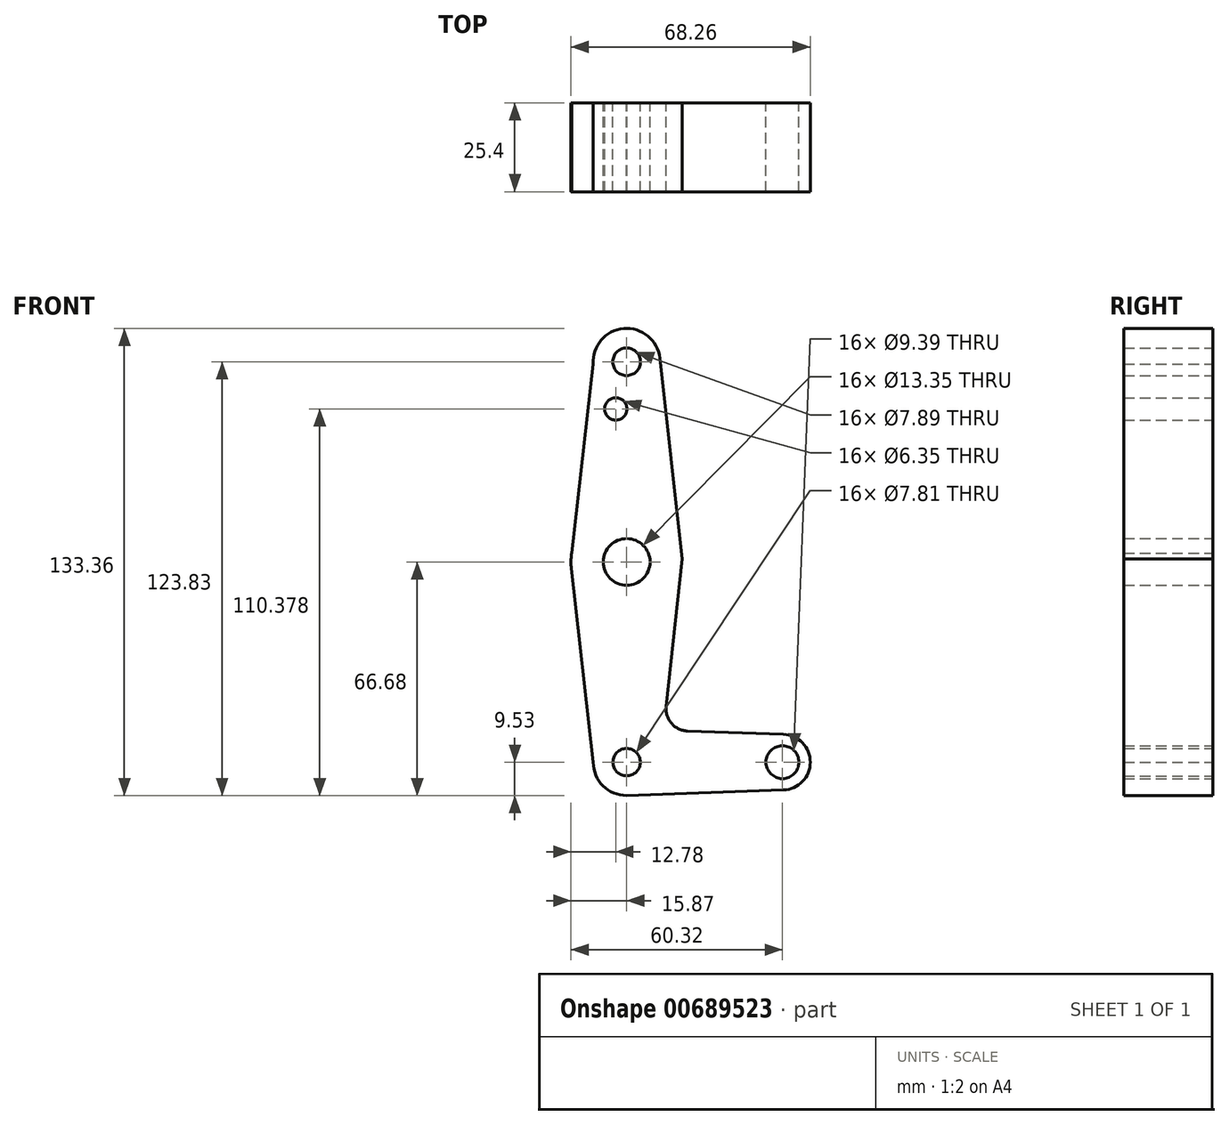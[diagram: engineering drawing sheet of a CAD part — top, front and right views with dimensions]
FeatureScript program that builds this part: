
annotation { "Feature Type Name" : "Feature", "Feature Type Description" : "" }
export const myFeature = defineFeature(function(context is Context, id is Id, definition is map)
    precondition{}
    {
        {
            var Q0;
            Q0=qCreatedBy(makeId("Front.planeOp"),FACE);
            var sketch = newSketch(context, id + "F0", { "sketchPlane" : qUnion([Q0])});
            skLineSegment(sketch, "E0", {"start": v(0, 0) * mm, "end": v(0, 114.3) * mm, "construction": true});
            skCircle(sketch, "E1", {"center": v(0, 114.3) * mm, "radius": 9.53 * mm});
            skCircle(sketch, "E2", {"center": v(0, 57.15) * mm, "radius": 15.88 * mm});
            skLineSegment(sketch, "E3", {"start": v(0, 0) * mm, "end": v(44.45, 0) * mm, "construction": true});
            skCircle(sketch, "E4", {"center": v(44.45, 0) * mm, "radius": 7.94 * mm});
            skCircle(sketch, "E5", {"center": v(0, 0) * mm, "radius": 9.53 * mm});
            skLineSegment(sketch, "E6", {"start": v(-9.52, 0) * mm, "end": v(-15.77, 55.37) * mm});
            skLineSegment(sketch, "E7", {"start": v(-15.68, 59.65) * mm, "end": v(-9.5, 113.65) * mm});
            skLineSegment(sketch, "E8", {"start": v(11.26, 15.94) * mm, "end": v(15.85, 58.03) * mm});
            skLineSegment(sketch, "E9", {"start": v(15.85, 58.03) * mm, "end": v(9.47, 115.35) * mm});
            skLineSegment(sketch, "E10", {"start": v(0, -9.53) * mm, "end": v(44.73, -7.93) * mm});
            skLineSegment(sketch, "E11", {"start": v(17.35, 8.9) * mm, "end": v(44.73, 7.93) * mm});
            skCircle(sketch, "E12", {"center": v(0, 114.3) * mm, "radius": 3.94 * mm});
            skCircle(sketch, "E13", {"center": v(-3.1, 100.85) * mm, "radius": 3.18 * mm});
            skCircle(sketch, "E14", {"center": v(0, 57.15) * mm, "radius": 6.68 * mm});
            skCircle(sketch, "E15", {"center": v(0, 0) * mm, "radius": 3.9 * mm});
            skCircle(sketch, "E16", {"center": v(44.45, 0) * mm, "radius": 4.7 * mm});
            skPoint(sketch, "E17.newPointB", {"position": v(0, 9.53) * mm});
            skArc(sketch, "E17.filletArc", {"start": v(11.26, 15.94) * mm, "mid": v(12.77, 11.1) * mm, "end": v(17.35, 8.9) * mm});
            skSolve(sketch);
        }
        {
            var Q0;
            {var subQ5=sQuery(id+"F0.wireOp",EDGE,"E7");Q0=makeQuery(id+"F0.imprint","IMPRINT",FACE,{"disambiguationData":[TD([[makeQuery(id+"F0.imprint","IMPRINT",EDGE,{"derivedFrom":subQ5}),-1.0]])]});}
            var Q1;
            Q1=makeQuery(id+"F0.imprint","IMPRINT",FACE,{"disambiguationData":[TD([[makeQuery(id+"F0.imprint","IMPRINT",EDGE,{"derivedFrom":sQuery(id+"F0.wireOp",EDGE,"E12")}),-1.0]])]});
            var Q2;
            Q2=makeQuery(id+"F0.imprint","IMPRINT",FACE,{"disambiguationData":[TD([[makeQuery(id+"F0.imprint","IMPRINT",EDGE,{"derivedFrom":sQuery(id+"F0.wireOp",EDGE,"E14")}),-1.0]])]});
            var Q3;
            {var subQ0=sQuery(id+"F0.wireOp",EDGE,"E6");Q3=makeQuery(id+"F0.imprint","IMPRINT",FACE,{"disambiguationData":[TD([[makeQuery(id+"F0.imprint","IMPRINT",EDGE,{"derivedFrom":subQ0}),-1.0]])]});}
            var Q4;
            Q4=makeQuery(id+"F0.imprint","IMPRINT",FACE,{"disambiguationData":[TD([[makeQuery(id+"F0.imprint","IMPRINT",EDGE,{"derivedFrom":sQuery(id+"F0.wireOp",EDGE,"E15")}),-1.0]])]});
            var Q5;
            Q5=makeQuery(id+"F0.imprint","IMPRINT",FACE,{"disambiguationData":[TD([[makeQuery(id+"F0.imprint","IMPRINT",EDGE,{"derivedFrom":sQuery(id+"F0.wireOp",EDGE,"E16")}),-1.0]])]});
            extrude(context, id + "F1", {"entities" : qUnion([Q0, Q1, Q2, Q3, Q4, Q5]), "depth" : 25.4 * mm, "offsetDistance" : 25.4 * mm});
        }
    });
